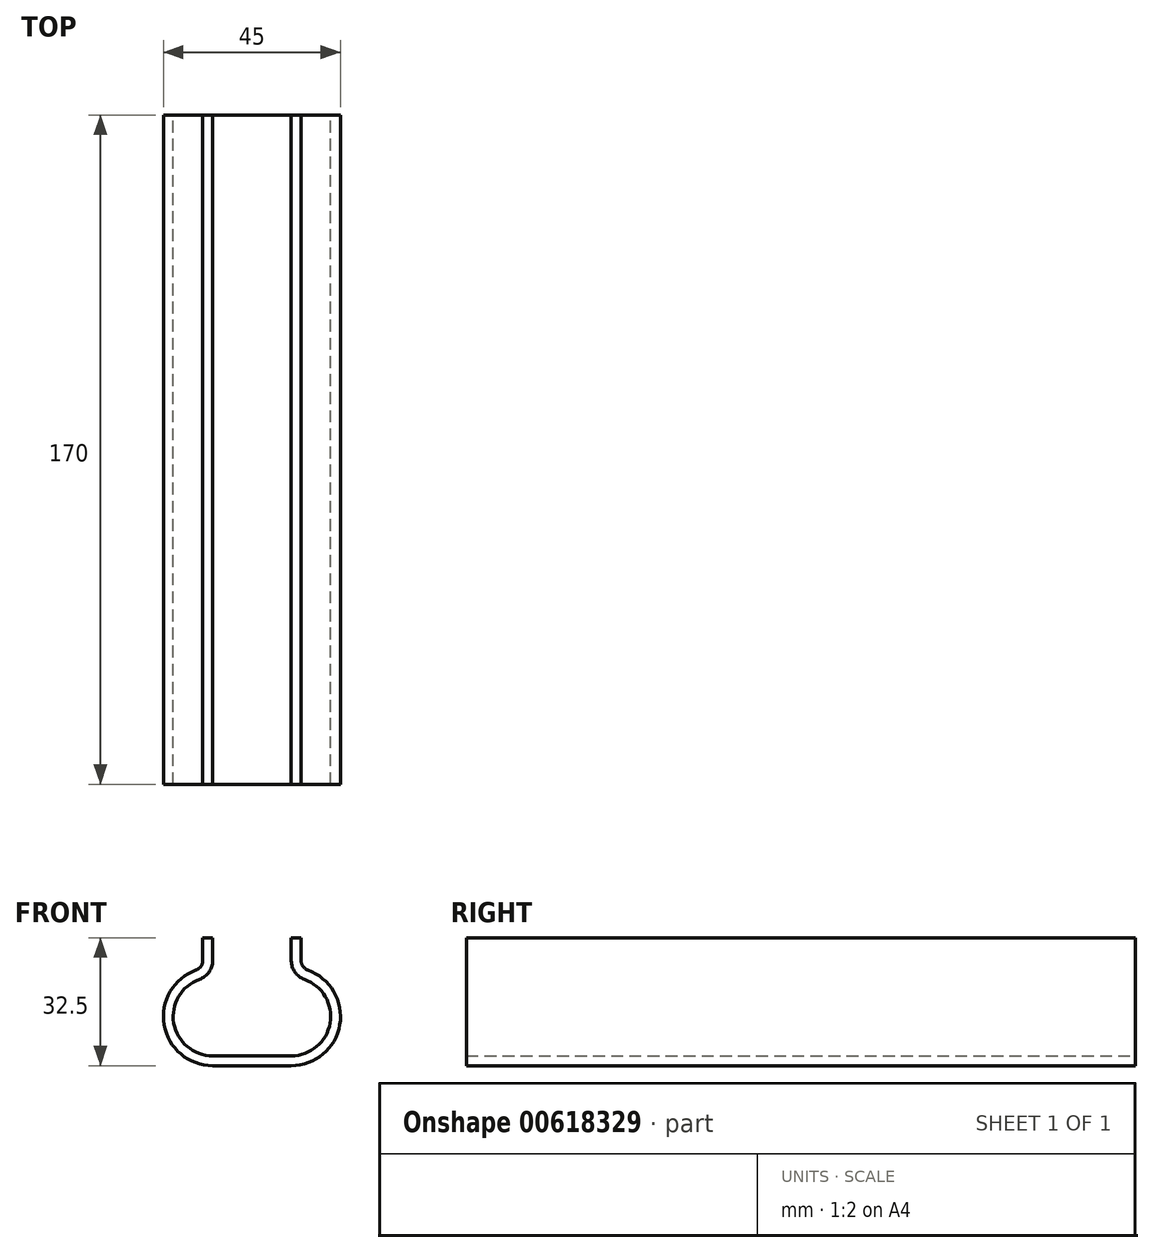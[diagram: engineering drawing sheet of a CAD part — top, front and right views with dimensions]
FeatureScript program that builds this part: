
annotation { "Feature Type Name" : "Feature", "Feature Type Description" : "" }
export const myFeature = defineFeature(function(context is Context, id is Id, definition is map)
    precondition{}
    {
        {
            var Q0;
            Q0=qCreatedBy(makeId("Front.planeOp"),FACE);
            var sketch = newSketch(context, id + "F0", { "sketchPlane" : qUnion([Q0])});
            skLineSegment(sketch, "E0", {"start": v(-10, 0) * mm, "end": v(-10, -5.86) * mm});
            skArc(sketch, "E1", {"start": v(-13.33, -10.57) * mm, "mid": v(-19.86, -21.7) * mm, "end": v(-10, -30) * mm});
            skArc(sketch, "E2", {"start": v(10, -30) * mm, "mid": v(19.86, -21.7) * mm, "end": v(13.33, -10.57) * mm});
            skLineSegment(sketch, "E3", {"start": v(-10, -30) * mm, "end": v(10, -30) * mm});
            skLineSegment(sketch, "E4", {"start": v(10, 0) * mm, "end": v(10, -5.86) * mm});
            skArc(sketch, "E5", {"start": v(10, -32.5) * mm, "mid": v(22.32, -22.11) * mm, "end": v(14.17, -8.21) * mm});
            skArc(sketch, "E6", {"start": v(-14.17, -8.21) * mm, "mid": v(-22.32, -22.11) * mm, "end": v(-10, -32.5) * mm});
            skLineSegment(sketch, "E7", {"start": v(-10, -32.5) * mm, "end": v(10, -32.5) * mm});
            skLineSegment(sketch, "E8", {"start": v(-10, 0) * mm, "end": v(-12.5, 0) * mm});
            skLineSegment(sketch, "E9", {"start": v(-12.5, 0) * mm, "end": v(-12.5, -5.86) * mm});
            skLineSegment(sketch, "E10", {"start": v(10, 0) * mm, "end": v(12.5, 0) * mm});
            skLineSegment(sketch, "E11", {"start": v(12.5, 0) * mm, "end": v(12.5, -5.86) * mm});
            skPoint(sketch, "E12.visualSharp", {"position": v(-10, -10) * mm});
            skArc(sketch, "E12.filletArc", {"start": v(-13.33, -10.57) * mm, "mid": v(-10.92, -8.74) * mm, "end": v(-10, -5.86) * mm});
            skPoint(sketch, "E13.visualSharp", {"position": v(-12.5, -7.75) * mm});
            skArc(sketch, "E13.filletArc", {"start": v(-14.17, -8.21) * mm, "mid": v(-12.96, -7.3) * mm, "end": v(-12.5, -5.86) * mm});
            skPoint(sketch, "E14.visualSharp", {"position": v(12.5, -7.75) * mm});
            skArc(sketch, "E14.filletArc", {"start": v(12.5, -5.86) * mm, "mid": v(12.96, -7.3) * mm, "end": v(14.17, -8.21) * mm});
            skPoint(sketch, "E15.visualSharp", {"position": v(10, -10) * mm});
            skArc(sketch, "E15.filletArc", {"start": v(10, -5.86) * mm, "mid": v(10.92, -8.74) * mm, "end": v(13.33, -10.57) * mm});
            skSolve(sketch);
        }
        {
            var Q0;
            Q0=makeQuery(id+"F0.imprint","IMPRINT",FACE,{"disambiguationData":[TD([[makeQuery(id+"F0.imprint","IMPRINT",EDGE,{"derivedFrom":sQuery(id+"F0.wireOp",EDGE,"E0")}),-1.0]])]});
            extrude(context, id + "F1", {"entities" : qUnion([Q0]), "depth" : 170 * mm, "offsetDistance" : 25 * mm});
        }
    });
